# Revit family: Berica S 2.0
name_source: partatom
category: Apparecchi per illuminazione
units: mm (PartAtom-declared; Revit-internal decimal feet)

## family parameters
Condiviso = No
Host = Controsoffitto
Numero OmniClass = 23.80.70.11
Punto di calcolo locali = Sì
Quota connettore circolare = Usa diametro
Sempre verticale = Sì
Sorgente d'illuminazione = No
Taglio con vuoti quando caricato = No
Tipo di parte = Normale
Titolo OmniClass = Luminaries for Internal Lighting

## types (3) — shared parameters
Base = L&L_Technopolymer
Bracket = L&L_Steel
CRI = CRI >90
Control system = ON/OFF, PUSH, DALI
Delivered lumen output = 776 lm (3000K, 44°x90°) down beam, 549 lm (3000K, diffuse) up beam
Descrizione = Suspended for indoor applications, double beam
Energy efficiency class = A A+ A++
Height mm = 120 mm  [stored 0.393701 ft]
IP = IP40
LED Colour = 2700K, 3000K, 4000K
Length mm = 620 mm  [stored 2.03412 ft]
Lens = L&L_PMMA
Light Source Up Berica 2.0 = Light Source Up Berica 2.0 : D
Lumen output at source = 941 lm (3000K) down beam, 706 lm (3000K) up beam
Material = body and cover in anticorodal aluminium, ceiling rose in steel
Middle = L&L_Anticorodal aluminium
Modello = Berica S 2.0
Mounting = surface mounted (ceiling)
No. and type of led = 84 mid-power LEDs, 3-step MacAdam, 60 000h L90 B10 (Ta 25°C)
Notes = non-standard lengths available on request, single-beam version available on request
Power = 14W
Power cables = includes 2.5 m PVC + PVC cable, 2x0.75 Ø5.4 mm,includes 2.5 m PVC + PVC cable, 5x0.75 Ø6.6 mm
includes 2.5 m PVC + PVC cable, 5x0.75 Ø6.6 mm
Power supply = 230Vac
Power supply unit = built-in
Produttore = L&L Luce&Light
Top = L&L_Anticorodal aluminium
URL = https://www.lucelight.it
URL Accessories and power supply units = https://www.lucelight.it
URL DXF = https://www.lucelight.it
URL Description = https://www.lucelight.it
URL General code = https://www.lucelight.it
URL IES Photometric file = https://www.lucelight.it
URL Image = https://www.lucelight.it
Weight kg = 2 kg
Width mm = 32 mm  [stored 0.104987 ft]
zero-valued in all types: Prospetto di default

## per-type parameters (varying)
| type | Light Source Down Berica 2.0 | Optics |
| BERICA S 2.0 D (3000K 14W 230Vac) DOWN | Light Source Down Berica 2.0 : D | Upper optics: diffuse / Lower optics: diffuse |
| BERICA S 2.0 K (3000K 14W 230Vac) DOWN | Light Source Down Berica 2.0 : K | Upper optics: diffuse / Lower optics: 44°x90° |
| BERICA S 2.0 L (3000K 14W 230Vac) DOWN | Light Source Down Berica 2.0 : L | Upper optics: diffuse / Lower optics: 58°x99° |

note: [stored X ft] marks values corroborated as IEEE doubles in the binary element streams (Revit-internal decimal feet)

## geometry (parser evidence)
native form markers: Blend x4, Sweep x8
no freeform markers — native parametric forms only
